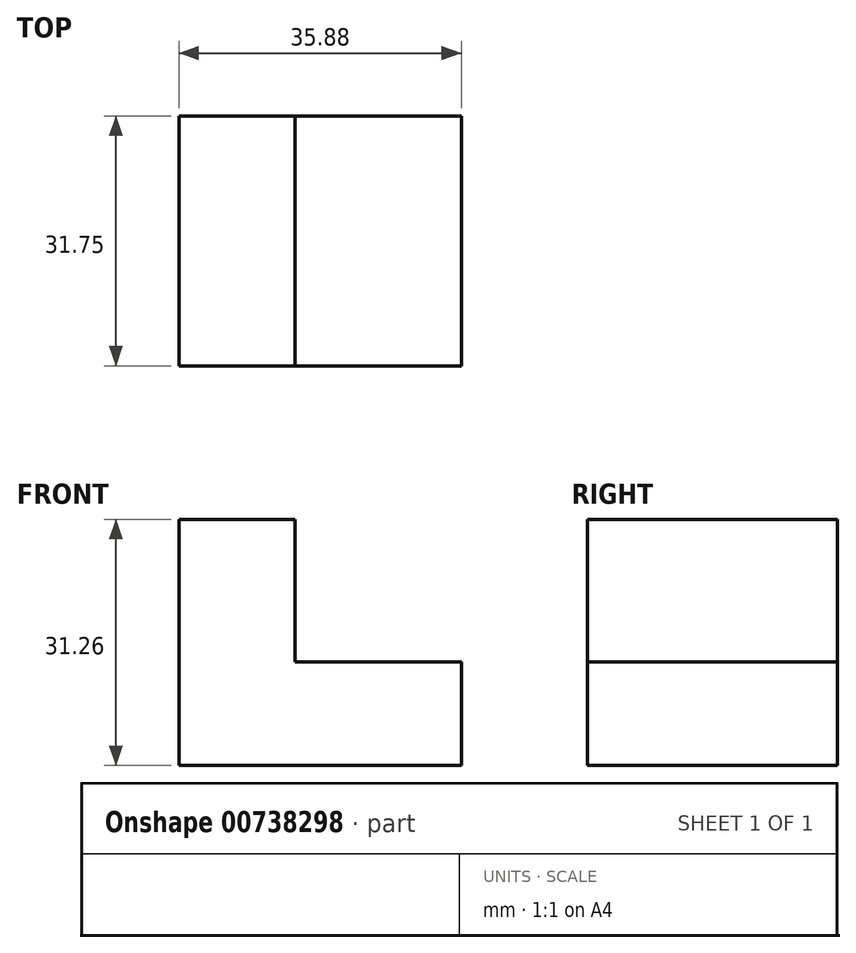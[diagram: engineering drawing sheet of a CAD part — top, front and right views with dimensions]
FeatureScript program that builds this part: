
annotation { "Feature Type Name" : "Feature", "Feature Type Description" : "" }
export const myFeature = defineFeature(function(context is Context, id is Id, definition is map)
    precondition{}
    {
        {
            var Q0;
            Q0=qCreatedBy(makeId("Front.planeOp"),FACE);
            var sketch = newSketch(context, id + "F0", { "sketchPlane" : qUnion([Q0])});
            skLineSegment(sketch, "E0", {"start": v(0, 0) * mm, "end": v(35.88, 0) * mm});
            skLineSegment(sketch, "E1", {"start": v(35.88, 0) * mm, "end": v(35.88, 13.17) * mm});
            skLineSegment(sketch, "E2", {"start": v(35.88, 13.17) * mm, "end": v(14.78, 13.17) * mm});
            skLineSegment(sketch, "E3", {"start": v(14.78, 13.17) * mm, "end": v(14.78, 31.26) * mm});
            skLineSegment(sketch, "E4", {"start": v(14.78, 31.26) * mm, "end": v(0, 31.26) * mm});
            skLineSegment(sketch, "E5", {"start": v(0, 31.26) * mm, "end": v(0, 0) * mm});
            skSolve(sketch);
        }
        {
            var Q0;
            Q0=makeQuery(id+"F0.imprint","IMPRINT",FACE,{"disambiguationData":[TD([[makeQuery(id+"F0.imprint","IMPRINT",EDGE,{"derivedFrom":sQuery(id+"F0.wireOp",EDGE,"E0")}),1.0]])]});
            extrude(context, id + "F1", {"entities" : qUnion([Q0]), "depth" : 31.75 * mm, "offsetDistance" : 25.4 * mm});
        }
    });
